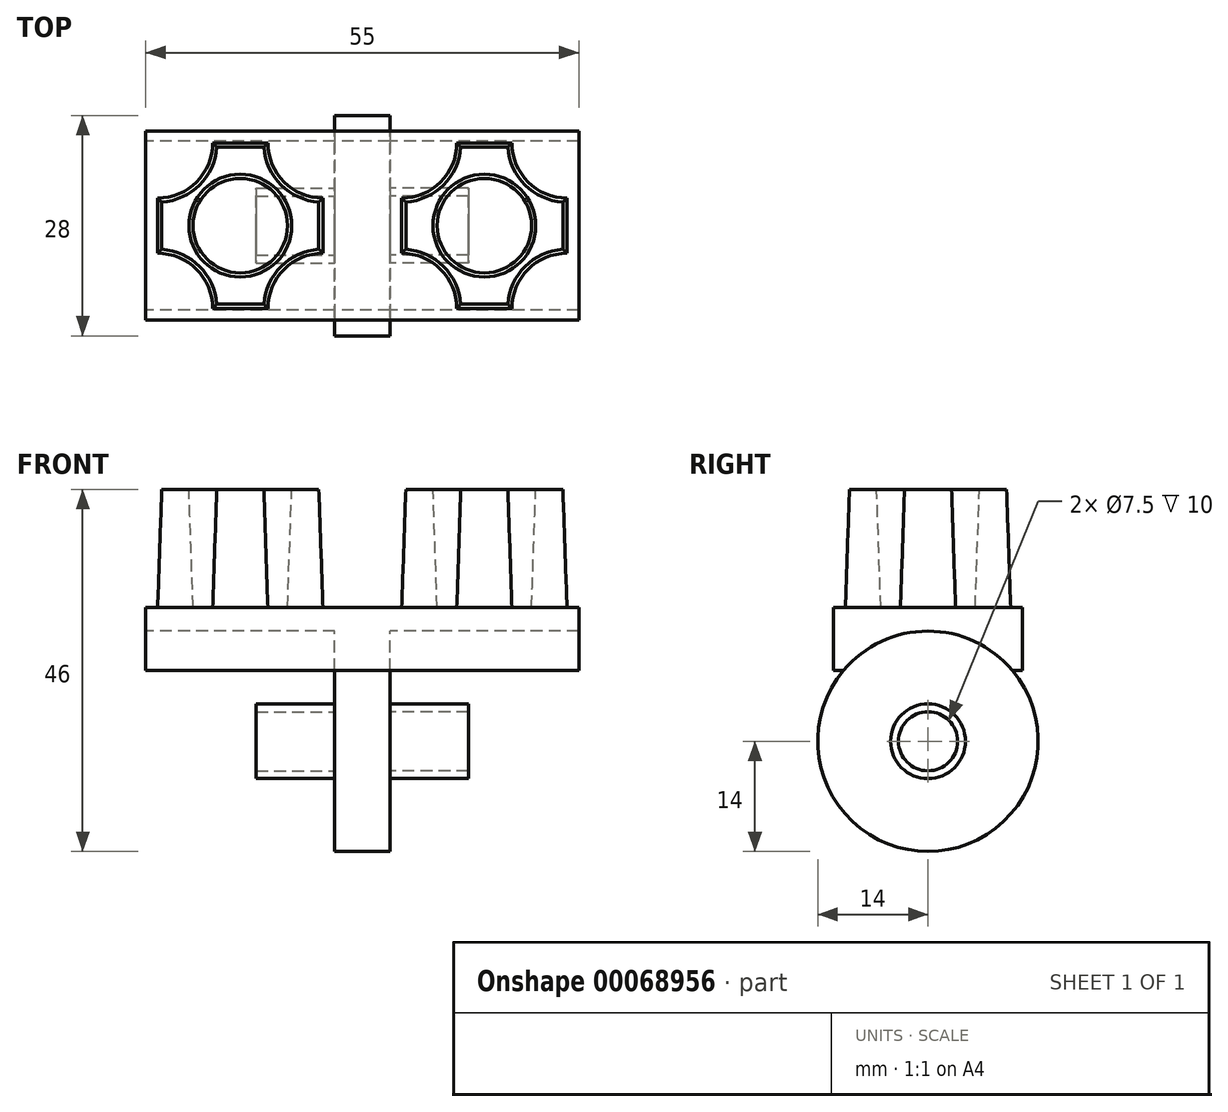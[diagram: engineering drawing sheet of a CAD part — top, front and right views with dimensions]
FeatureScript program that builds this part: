
annotation { "Feature Type Name" : "Feature", "Feature Type Description" : "" }
export const myFeature = defineFeature(function(context is Context, id is Id, definition is map)
    precondition{}
    {
        {
            var Q0;
            Q0=qCreatedBy(makeId("Top.planeOp"),FACE);
            var sketch = newSketch(context, id + "F0", { "sketchPlane" : qUnion([Q0])});
            skLineSegment(sketch, "E0.rect.bottom", {"start": v(27.5, -12) * mm, "end": v(-27.5, -12) * mm});
            skLineSegment(sketch, "E0.rect.top", {"start": v(27.5, 12) * mm, "end": v(-27.5, 12) * mm});
            skLineSegment(sketch, "E0.rect.left", {"start": v(27.5, -12) * mm, "end": v(27.5, 12) * mm});
            skLineSegment(sketch, "E0.rect.right", {"start": v(-27.5, -12) * mm, "end": v(-27.5, 12) * mm});
            skPoint(sketch, "E0.rect.middle", {"position": v(0, 0) * mm});
            skSolve(sketch);
        }
        {
            var Q0;
            Q0 = qSketchRegion(id + "F0", true);
            extrude(context, id + "F1", {"entities" : qUnion([Q0]), "depth" : 8 * mm});
        }
        {
            var Q0;
            Q0=makeQuery(id+"F1.opExtrude","SWEPT_FACE",FACE,{"disambiguationData":[OSD([sQuery(id+"F0.wireOp",EDGE,"E0.rect.right")])]});
            var sketch = newSketch(context, id + "F2", { "sketchPlane" : qUnion([Q0])});
            skCircle(sketch, "E1", {"center": v(0, -9) * mm, "radius": 14 * mm});
            skPoint(sketch, "E1.centerSnap0", {"position": v(0, 0) * mm});
            skSolve(sketch);
        }
        {
            var Q0;
            {var subQ0=sQuery(id+"F2.wireOp",EDGE,"E1");var subQ1=makeQuery(id+"F1.opExtrude","CAP_EDGE",EDGE,{"disambiguationData":[OSD([sQuery(id+"F0.wireOp",EDGE,"E0.rect.right")])],"isStart":true});var subQ2=makeQuery(id+"F2.imprint","INTERSECT",VERTEX,{"disambiguationData":[OD(0.0)],"derivedFrom":[subQ1,subQ0]});Q0=makeQuery(id+"F2.imprint","IMPRINT",FACE,{"disambiguationData":[TD([[makeQuery(id+"F2.imprint","IMPRINT",EDGE,{"disambiguationData":[TD([[subQ2,-1.0]])],"derivedFrom":subQ0}),1.0]])]});}
            var Q1;
            {var subQ0=sQuery(id+"F2.wireOp",EDGE,"E1");var subQ1=makeQuery(id+"F1.opExtrude","CAP_EDGE",EDGE,{"disambiguationData":[OSD([sQuery(id+"F0.wireOp",EDGE,"E0.rect.right")])],"isStart":true});var subQ2=makeQuery(id+"F2.imprint","INTERSECT",VERTEX,{"disambiguationData":[OD(0.0)],"derivedFrom":[subQ1,subQ0]});Q1=makeQuery(id+"F2.imprint","IMPRINT",FACE,{"disambiguationData":[TD([[makeQuery(id+"F2.imprint","IMPRINT",EDGE,{"disambiguationData":[TD([[subQ2,1.0]])],"derivedFrom":subQ0}),1.0]])]});}
            extrude(context, id + "F3", {"entities" : qUnion([Q0, Q1]), "operationType" : NewBodyOperationType.REMOVE, "oppositeDirection" : true, "depth" : 62.04 * mm});
        }
        {
            var Q0;
            Q0=qCreatedBy(makeId("Right.planeOp"),FACE);
            var sketch = newSketch(context, id + "F4", { "sketchPlane" : qUnion([Q0])});
            skCircle(sketch, "E2", {"center": v(0, -9) * mm, "radius": 14 * mm});
            skSolve(sketch);
        }
        {
            var Q0;
            Q0=makeQuery(id+"F4.imprint","IMPRINT",FACE,{"disambiguationData":[TD([[makeQuery(id+"F4.imprint","IMPRINT",EDGE,{"derivedFrom":sQuery(id+"F4.wireOp",EDGE,"E2")}),1.0]])]});
            extrude(context, id + "F5", {"entities" : qUnion([Q0]), "operationType" : NewBodyOperationType.ADD, "depth" : 3.5 * mm, "hasSecondDirection" : true, "secondDirectionOppositeDirection" : true, "secondDirectionDepth" : 3.5 * mm});
        }
        {
            var Q0;
            Q0=makeQuery(id+"F5.opExtrude","CAP_FACE",FACE,{"disambiguationData":[OSD([sQuery(id+"F4.wireOp",EDGE,"E2")])],"isStart":false});
            var sketch = newSketch(context, id + "F6", { "sketchPlane" : qUnion([Q0])});
            skSolve(sketch);
        }
        {
            var Q0;
            {var subQ0=makeQuery(id+"F5.opExtrude","CAP_EDGE",EDGE,{"disambiguationData":[OSD([sQuery(id+"F4.wireOp",EDGE,"E2")])],"isStart":false});Q0=makeQuery(id+"F6.imprint","IMPRINT",FACE,{"disambiguationData":[TD([[makeQuery(id+"F6.imprint","IMPRINT",EDGE,{"derivedFrom":makeQuery(id+"F5.boolean.opBoolean","SPLIT",EDGE,{"disambiguationData":[OD(0.0)],"derivedFrom":subQ0})}),1.0]])]});}
            var sketch = newSketch(context, id + "F7", { "sketchPlane" : qUnion([Q0])});
            skCircle(sketch, "E3", {"center": v(0, -9) * mm, "radius": 3.75 * mm});
            skCircle(sketch, "E4", {"center": v(0, -9) * mm, "radius": 4.75 * mm});
            skSolve(sketch);
        }
        {
            var Q0;
            Q0 = qSketchRegion(id + "F7", true);
            extrude(context, id + "F8", {"entities" : qUnion([Q0]), "operationType" : NewBodyOperationType.ADD, "depth" : 10 * mm});
        }
        {
            var Q0;
            Q0=makeQuery(id+"F1.opExtrude","SWEPT_BODY",BODY,{"disambiguationData":[OSD([sQuery(id+"F0.wireOp",EDGE,"E0.rect.bottom"),sQuery(id+"F0.wireOp",EDGE,"E0.rect.top"),sQuery(id+"F0.wireOp",EDGE,"E0.rect.left"),sQuery(id+"F0.wireOp",EDGE,"E0.rect.right")])]});
            var Q1;
            Q1=qCreatedBy(makeId("Right.planeOp"),FACE);
            mirror(context, id + "F9", {"operationType" : NewBodyOperationType.ADD, "entities" : qUnion([Q0]), "mirrorPlane" : qUnion([Q1])});
        }
        {
            var Q0;
            Q0=makeQuery(id+"F1.opExtrude","CAP_FACE",FACE,{"disambiguationData":[OSD([sQuery(id+"F0.wireOp",EDGE,"E0.rect.bottom"),sQuery(id+"F0.wireOp",EDGE,"E0.rect.top"),sQuery(id+"F0.wireOp",EDGE,"E0.rect.left"),sQuery(id+"F0.wireOp",EDGE,"E0.rect.right")])],"isStart":false});
            var sketch = newSketch(context, id + "F10", { "sketchPlane" : qUnion([Q0])});
            skLineSegment(sketch, "E5.rect.bottom", {"start": v(12, 10.5) * mm, "end": v(19, 10.5) * mm});
            skLineSegment(sketch, "E5.rect.top", {"start": v(12, -10.5) * mm, "end": v(19, -10.5) * mm});
            skLineSegment(sketch, "E5.rect.left", {"start": v(5, 3.5) * mm, "end": v(5, -3.5) * mm});
            skLineSegment(sketch, "E5.rect.right", {"start": v(26, 3.5) * mm, "end": v(26, -3.5) * mm});
            skPoint(sketch, "E5.rect.middle", {"position": v(15.5, 0) * mm});
            skArc(sketch, "E6", {"start": v(26, -3.5) * mm, "mid": v(21.05, -5.55) * mm, "end": v(19, -10.5) * mm});
            skArc(sketch, "E7", {"start": v(19, 10.5) * mm, "mid": v(21.05, 5.55) * mm, "end": v(26, 3.5) * mm});
            skArc(sketch, "E8", {"start": v(12, -10.5) * mm, "mid": v(9.95, -5.55) * mm, "end": v(5, -3.5) * mm});
            skArc(sketch, "E9", {"start": v(5, 3.5) * mm, "mid": v(9.95, 5.55) * mm, "end": v(12, 10.5) * mm});
            skCircle(sketch, "E10", {"center": v(15.5, 0) * mm, "radius": 6 * mm});
            skSolve(sketch);
        }
        {
            var Q0;
            Q0=makeQuery(id+"F10.imprint","IMPRINT",FACE,{"disambiguationData":[TD([[makeQuery(id+"F10.imprint","IMPRINT",EDGE,{"derivedFrom":sQuery(id+"F10.wireOp",EDGE,"E5.rect.bottom")}),-1.0]])]});
            extrude(context, id + "F11", {"entities" : qUnion([Q0]), "operationType" : NewBodyOperationType.ADD, "depth" : 15 * mm, "hasDraft" : true, "draftAngle" : 2 * degree, "draftPullDirection" : true});
        }
        {
            var Q0;
            Q0=makeQuery(id+"F1.opExtrude","SWEPT_BODY",BODY,{"disambiguationData":[OSD([sQuery(id+"F0.wireOp",EDGE,"E0.rect.bottom"),sQuery(id+"F0.wireOp",EDGE,"E0.rect.top"),sQuery(id+"F0.wireOp",EDGE,"E0.rect.left"),sQuery(id+"F0.wireOp",EDGE,"E0.rect.right")])]});
            var Q1;
            Q1=qCreatedBy(makeId("Right.planeOp"),FACE);
            mirror(context, id + "F12", {"operationType" : NewBodyOperationType.ADD, "entities" : qUnion([Q0]), "mirrorPlane" : qUnion([Q1])});
        }
    });
